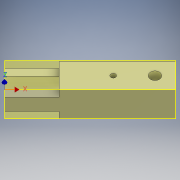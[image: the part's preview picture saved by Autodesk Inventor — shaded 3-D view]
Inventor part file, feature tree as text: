
AUTODESK INVENTOR PART (.ipt)
format: ipt  version: 2018 (Build 220112000, 112)  size: 417,280 bytes
history: native  units: in
note: dims shown in document units (in); Inventor stores cm internally (conversion verified against a paired STEP export)
features: extrude x5, sketch x5
ambient origin geometry x8: Origin, YZ Plane, XZ Plane, XY Plane, X Axis, Y Axis, Z Axis, Center Point
bodies: Solid1 (feature_tree)
feature tree (10):
  extrude  "Extrusion1"  Depth=0.74in
  extrude  "Extrusion2"  Depth=0.25in
  extrude  "Extrusion3"  Depth=0.375in
  extrude  "Extrusion4"  Depth=0.74in
  extrude  "Extrusion5"  Depth=2.125in
  sketch  "Sketch1"  dims[d0=0.74in d1=3.125in]
  sketch  "Sketch2"  dims[d2=0.74in d3=0.0in d4=0.25in]
  sketch  "Sketch3"  dims[d5=0.37in d6=0.375in]
  sketch  "Sketch4"  dims[d7=0.74in d8=0.0in d9=0.125in]
  sketch  "Sketch5"  dims[d10=0.37in d11=1.137in d12=0.37in d13=0.0in d14=0.5in d15=0.37in d16=0.37in d17=2.125in d18=0.0in d19=2.125in d20=0.187in d21=0.187in d22=0.0in d23=2.125in d24=0.0in]
